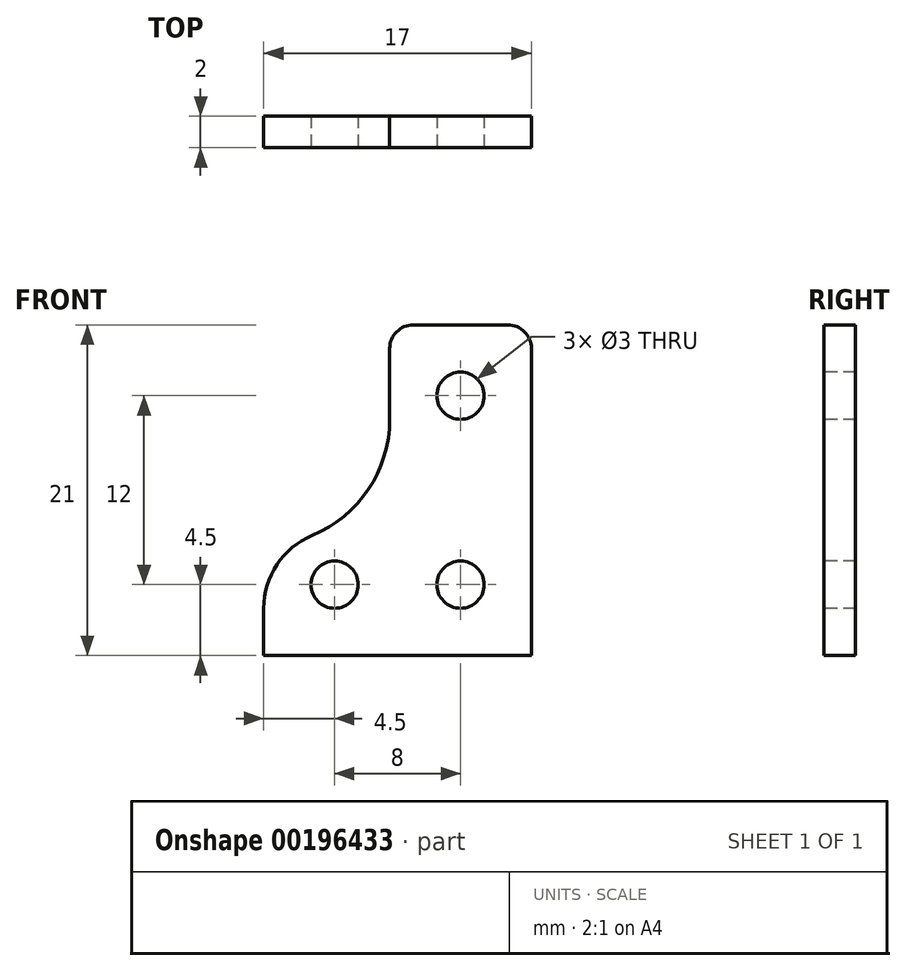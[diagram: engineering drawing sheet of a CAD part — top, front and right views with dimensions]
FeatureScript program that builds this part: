
annotation { "Feature Type Name" : "Feature", "Feature Type Description" : "" }
export const myFeature = defineFeature(function(context is Context, id is Id, definition is map)
    precondition{}
    {
        {
            var Q0;
            Q0=qCreatedBy(makeId("Front.planeOp"),FACE);
            var sketch = newSketch(context, id + "F0", { "sketchPlane" : qUnion([Q0])});
            skLineSegment(sketch, "E0.bottom", {"start": v(8.5, 7.5) * mm, "end": v(-8.5, 7.5) * mm});
            skLineSegment(sketch, "E0.top", {"start": v(8.5, -7.5) * mm, "end": v(-8.5, -7.5) * mm});
            skLineSegment(sketch, "E0.left", {"start": v(8.5, 7.5) * mm, "end": v(8.5, -7.5) * mm});
            skLineSegment(sketch, "E0.right", {"start": v(-8.5, 7.5) * mm, "end": v(-8.5, -7.5) * mm});
            skPoint(sketch, "E0.middle", {"position": v(0, 0) * mm});
            skSolve(sketch);
        }
        {
            var Q0;
            Q0=qSketchRegion(id+"F0",true);
            extrude(context, id + "F1", {"entities" : qUnion([Q0]), "depth" : 2 * mm});
        }
        {
            var Q0;
            Q0=makeQuery(id+"F1.opExtrude","CAP_FACE",FACE,{"disambiguationData":[OSD([sQuery(id+"F0.wireOp",EDGE,"E0.bottom"),sQuery(id+"F0.wireOp",EDGE,"E0.top"),sQuery(id+"F0.wireOp",EDGE,"E0.left"),sQuery(id+"F0.wireOp",EDGE,"E0.right")])],"isStart":false});
            var sketch = newSketch(context, id + "F2", { "sketchPlane" : qUnion([Q0])});
            skCircle(sketch, "E1", {"center": v(4, 3) * mm, "radius": 1.5 * mm, "construction": true});
            skCircle(sketch, "E2", {"center": v(-4, 3) * mm, "radius": 1.5 * mm, "construction": true});
            skCircle(sketch, "E3", {"center": v(-4, -3) * mm, "radius": 1.5 * mm});
            skCircle(sketch, "E4", {"center": v(4, -3) * mm, "radius": 1.5 * mm});
            skSolve(sketch);
        }
        {
            var Q0;
            Q0=qSketchRegion(id+"F2",true);
            extrude(context, id + "F3", {"entities" : qUnion([Q0]), "operationType" : NewBodyOperationType.REMOVE, "oppositeDirection" : true, "depth" : 25 * mm});
        }
        {
            var Q0;
            Q0=makeQuery(id+"F1.opExtrude","SWEPT_FACE",FACE,{"disambiguationData":[OSD([sQuery(id+"F0.wireOp",EDGE,"E0.bottom")])]});
            var sketch = newSketch(context, id + "F4", { "sketchPlane" : qUnion([Q0])});
            skLineSegment(sketch, "E5.bottom", {"start": v(8.5, 0) * mm, "end": v(-0.5, 0) * mm});
            skLineSegment(sketch, "E5.top", {"start": v(8.5, -2) * mm, "end": v(-0.5, -2) * mm});
            skLineSegment(sketch, "E5.left", {"start": v(8.5, 0) * mm, "end": v(8.5, -2) * mm});
            skLineSegment(sketch, "E5.right", {"start": v(-0.5, 0) * mm, "end": v(-0.5, -2) * mm});
            skSolve(sketch);
        }
        {
            var Q0;
            Q0=qSketchRegion(id+"F4",true);
            extrude(context, id + "F5", {"entities" : qUnion([Q0]), "operationType" : NewBodyOperationType.ADD, "depth" : 6 * mm});
        }
        {
            var Q0;
            Q0=makeQuery(id+"F5.boolean.opBoolean","MERGE",FACE,{"derivedFrom":[makeQuery(id+"F1.opExtrude","CAP_FACE",FACE,{"disambiguationData":[OSD([sQuery(id+"F0.wireOp",EDGE,"E0.bottom"),sQuery(id+"F0.wireOp",EDGE,"E0.top"),sQuery(id+"F0.wireOp",EDGE,"E0.left"),sQuery(id+"F0.wireOp",EDGE,"E0.right")])],"isStart":false}),makeQuery(id+"F5.opExtrude","SWEPT_FACE",FACE,{"disambiguationData":[OSD([sQuery(id+"F4.wireOp",EDGE,"E5.top")])]})]});
            var sketch = newSketch(context, id + "F6", { "sketchPlane" : qUnion([Q0])});
            skCircle(sketch, "E6", {"center": v(4, 9) * mm, "radius": 1.5 * mm});
            skSolve(sketch);
        }
        {
            var Q0;
            Q0=qSketchRegion(id+"F6",true);
            extrude(context, id + "F7", {"entities" : qUnion([Q0]), "operationType" : NewBodyOperationType.REMOVE, "oppositeDirection" : true, "depth" : 25 * mm});
        }
        {
            var Q0;
            Q0=makeQuery(id+"F5.opExtrude","CAP_EDGE",EDGE,{"disambiguationData":[OSD([sQuery(id+"F4.wireOp",EDGE,"E5.left")])],"isStart":false});
            var Q1;
            Q1=makeQuery(id+"F5.opExtrude","CAP_EDGE",EDGE,{"disambiguationData":[OSD([sQuery(id+"F4.wireOp",EDGE,"E5.right")])],"isStart":false});
            fillet(context, id + "F8", {"entities" : qUnion([Q0, Q1]), "radius" : 1.5 * mm, "tangentPropagation" : true, "allowEdgeOverflow" : false});
        }
        {
            var Q0;
            Q0=makeQuery(id+"F1.opExtrude","SWEPT_FACE",FACE,{"disambiguationData":[OSD([sQuery(id+"F0.wireOp",EDGE,"E0.top")])]});
            var sketch = newSketch(context, id + "F9", { "sketchPlane" : qUnion([Q0])});
            skLineSegment(sketch, "E7.bottom", {"start": v(-8.5, 2) * mm, "end": v(8.5, 2) * mm});
            skLineSegment(sketch, "E7.top", {"start": v(-8.5, 0) * mm, "end": v(8.5, 0) * mm});
            skLineSegment(sketch, "E7.left", {"start": v(-8.5, 2) * mm, "end": v(-8.5, 0) * mm});
            skLineSegment(sketch, "E7.right", {"start": v(8.5, 2) * mm, "end": v(8.5, 0) * mm});
            skSolve(sketch);
        }
        {
            var Q0;
            Q0=qSketchRegion(id+"F9",true);
            extrude(context, id + "F10", {"entities" : qUnion([Q0]), "operationType" : NewBodyOperationType.ADD, "depth" : 1 * mm});
        }
        {
            var Q0;
            Q0=makeQuery(id+"F10.opExtrude","CAP_FACE",FACE,{"disambiguationData":[OSD([sQuery(id+"F9.wireOp",EDGE,"E7.bottom"),sQuery(id+"F9.wireOp",EDGE,"E7.top"),sQuery(id+"F9.wireOp",EDGE,"E7.left"),sQuery(id+"F9.wireOp",EDGE,"E7.right")])],"isStart":false});
            var sketch = newSketch(context, id + "F11", { "sketchPlane" : qUnion([Q0])});
            skLineSegment(sketch, "E8.bottom", {"start": v(-8.5, 2) * mm, "end": v(8.5, 2) * mm});
            skLineSegment(sketch, "E8.top", {"start": v(-8.5, -4) * mm, "end": v(8.5, -4) * mm});
            skLineSegment(sketch, "E8.left", {"start": v(-8.5, 2) * mm, "end": v(-8.5, -4) * mm});
            skLineSegment(sketch, "E8.right", {"start": v(8.5, 2) * mm, "end": v(8.5, -4) * mm});
            skSolve(sketch);
        }
        {
            var Q0;
            Q0=qSketchRegion(id+"F11",true);
            extrude(context, id + "F12", {"entities" : qUnion([Q0]), "operationType" : NewBodyOperationType.ADD, "depth" : 8 * mm});
        }
        {
            var Q0;
            Q0=makeQuery(id+"F12.opExtrude","SWEPT_FACE",FACE,{"disambiguationData":[OSD([sQuery(id+"F11.wireOp",EDGE,"E8.top")])]});
            var sketch = newSketch(context, id + "F13", { "sketchPlane" : qUnion([Q0])});
            skLineSegment(sketch, "E9.bottom", {"start": v(-8.5, -8.5) * mm, "end": v(8.5, -8.5) * mm});
            skLineSegment(sketch, "E9.top", {"start": v(-8.5, -16.5) * mm, "end": v(8.5, -16.5) * mm});
            skLineSegment(sketch, "E9.left", {"start": v(-8.5, -8.5) * mm, "end": v(-8.5, -16.5) * mm});
            skLineSegment(sketch, "E9.right", {"start": v(8.5, -8.5) * mm, "end": v(8.5, -16.5) * mm});
            skSolve(sketch);
        }
        {
            var Q0;
            Q0 = qSketchRegion(id + "F13", true);
            extrude(context, id + "F14", {"entities" : qUnion([Q0]), "operationType" : NewBodyOperationType.REMOVE, "oppositeDirection" : true, "depth" : 25 * mm});
        }
        {
            var Q0;
            Q0=makeQuery(id+"F14.boolean.opBoolean","COPY",FACE,{"derivedFrom":makeQuery(id+"F14.opExtrude","SWEPT_FACE",FACE,{"disambiguationData":[OSD([sQuery(id+"F13.wireOp",EDGE,"E9.bottom")])]})});
            var sketch = newSketch(context, id + "F15", { "sketchPlane" : qUnion([Q0])});
            skLineSegment(sketch, "E10.bottom", {"start": v(-8.5, 2) * mm, "end": v(8.5, 2) * mm});
            skLineSegment(sketch, "E10.top", {"start": v(-8.5, 0) * mm, "end": v(8.5, 0) * mm});
            skLineSegment(sketch, "E10.left", {"start": v(-8.5, 2) * mm, "end": v(-8.5, 0) * mm});
            skLineSegment(sketch, "E10.right", {"start": v(8.5, 2) * mm, "end": v(8.5, 0) * mm});
            skSolve(sketch);
        }
        {
            var Q0;
            Q0 = qSketchRegion(id + "F15", true);
            extrude(context, id + "F16", {"entities" : qUnion([Q0]), "operationType" : NewBodyOperationType.REMOVE, "oppositeDirection" : true, "depth" : 1 * mm});
        }
        {
            var Q0;
            Q0=makeQuery(id+"F10.boolean.opBoolean","MERGE",FACE,{"derivedFrom":[makeQuery(id+"F5.boolean.opBoolean","MERGE",FACE,{"derivedFrom":[makeQuery(id+"F1.opExtrude","CAP_FACE",FACE,{"disambiguationData":[OSD([sQuery(id+"F0.wireOp",EDGE,"E0.bottom"),sQuery(id+"F0.wireOp",EDGE,"E0.top"),sQuery(id+"F0.wireOp",EDGE,"E0.left"),sQuery(id+"F0.wireOp",EDGE,"E0.right")])],"isStart":true}),makeQuery(id+"F5.opExtrude","SWEPT_FACE",FACE,{"disambiguationData":[OSD([sQuery(id+"F4.wireOp",EDGE,"E5.bottom")])]})]}),makeQuery(id+"F10.opExtrude","SWEPT_FACE",FACE,{"disambiguationData":[OSD([sQuery(id+"F9.wireOp",EDGE,"E7.top")])]})]});
            var sketch = newSketch(context, id + "F17", { "sketchPlane" : qUnion([Q0])});
            skCircle(sketch, "E11", {"center": v(8.5, 7.5) * mm, "radius": 8 * mm});
            skSolve(sketch);
        }
        {
            var Q0;
            Q0 = qSketchRegion(id + "F17", true);
            extrude(context, id + "F18", {"entities" : qUnion([Q0]), "operationType" : NewBodyOperationType.REMOVE, "oppositeDirection" : true, "depth" : 25 * mm});
        }
        {
            var Q0;
            Q0=makeQuery(id+"F18.boolean.opBoolean","INTERSECT",EDGE,{"derivedFrom":[makeQuery(id+"F12.boolean.opBoolean","MERGE",FACE,{"derivedFrom":[makeQuery(id+"F10.boolean.opBoolean","MERGE",FACE,{"derivedFrom":[makeQuery(id+"F1.opExtrude","SWEPT_FACE",FACE,{"disambiguationData":[OSD([sQuery(id+"F0.wireOp",EDGE,"E0.right")])]}),makeQuery(id+"F10.opExtrude","SWEPT_FACE",FACE,{"disambiguationData":[OSD([sQuery(id+"F9.wireOp",EDGE,"E7.left")])]})]}),makeQuery(id+"F12.opExtrude","SWEPT_FACE",FACE,{"disambiguationData":[OSD([sQuery(id+"F11.wireOp",EDGE,"E8.left")])]})]}),makeQuery(id+"F18.opExtrude","SWEPT_FACE",FACE,{"disambiguationData":[OSD([sQuery(id+"F17.wireOp",EDGE,"E11")])]})]});
            fillet(context, id + "F19", {"entities" : qUnion([Q0]), "radius" : 5 * mm, "tangentPropagation" : true, "allowEdgeOverflow" : false});
        }
    });
